# Revit family: Haworth_BuzziProp_Pendant
name_source: partatom
category: Lighting Fixtures
revit_build: Autodesk Revit 2018 (Build: 20170223_1515(x64)
units: mm (PartAtom-declared; Revit-internal decimal feet)

## family parameters
Cut with Voids When Loaded = No
Host = Face
Light Source = No
Part Type = Normal
Room Calculation Point = No
Round Connector Dimension = Use Diameter
Shared = No

## types (1)
- HCBZ-PRP
    Actual Depth = 17.72 "
    Actual Height = 17.72 "
    Actual Width = 17.72 "
    Assembly Code = E2020200
    Default Elevation = 0 "
    Description = Haworth BuzziProp LED Pendant Light
    Glass Finish = Haworth _ Glass _ Frosted
    Manufacturer = Haworth
    Max. Cable Length = 196.85 "
    Min. Cable Length = 10 "
    Model = HCBZ-PRP
    Note = Verify Final Dim. w/ Haworth
    Revision = 1
    Trim Finish = Haworth _ Paint _ Collection Black
    URL = http://www.haworth.com
    URL - Product = https://www.haworth.com
    Warranty = http://www.haworth.com

## geometry (parser evidence)
native form markers: Sweep x3
no freeform markers — native parametric forms only
